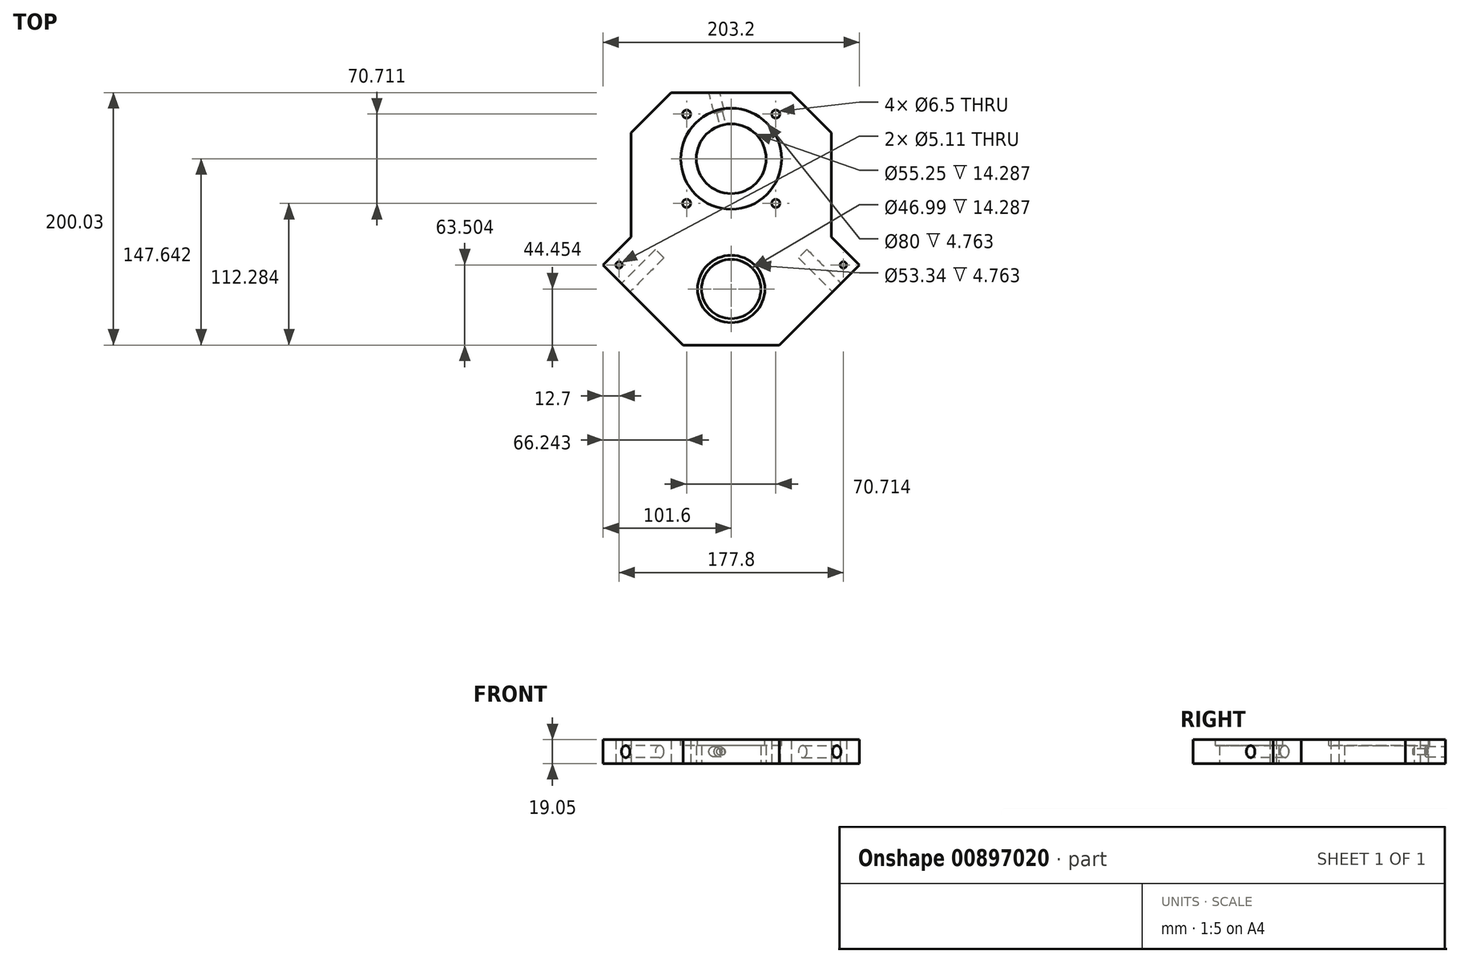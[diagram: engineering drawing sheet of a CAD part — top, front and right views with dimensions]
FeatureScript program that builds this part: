
annotation { "Feature Type Name" : "Feature", "Feature Type Description" : "" }
export const myFeature = defineFeature(function(context is Context, id is Id, definition is map)
    precondition{}
    {
        {
            var Q0;
            Q0=qCreatedBy(makeId("Top.planeOp"),FACE);
            var sketch = newSketch(context, id + "F0", { "sketchPlane" : qUnion([Q0])});
            skCircle(sketch, "E0", {"center": v(0, 19.05) * mm, "radius": 27.62 * mm});
            skPoint(sketch, "E0.centerSnap0", {"position": v(0, 71.44) * mm});
            skPoint(sketch, "E1", {"position": v(101.6, 0) * mm});
            skLineSegment(sketch, "E2", {"start": v(0, 71.44) * mm, "end": v(-47.63, 71.44) * mm});
            skLineSegment(sketch, "E3", {"start": v(-47.63, 71.44) * mm, "end": v(-79.38, 39.69) * mm});
            skPoint(sketch, "E4.orphan", {"position": v(-79.38, 71.44) * mm});
            skLineSegment(sketch, "E5", {"start": v(-79.38, 39.69) * mm, "end": v(-79.38, -42.86) * mm});
            skLineSegment(sketch, "E6", {"start": v(-101.6, -65.09) * mm, "end": v(-79.37, -42.86) * mm});
            skLineSegment(sketch, "E7", {"start": v(-101.6, -65.09) * mm, "end": v(-38.1, -128.59) * mm});
            skLineSegment(sketch, "E8", {"start": v(-38.1, -128.59) * mm, "end": v(0, -128.59) * mm});
            skLineSegment(sketch, "E9.MirrorCS", {"start": v(38.1, -128.59) * mm, "end": v(0, -128.59) * mm});
            skLineSegment(sketch, "E10.MirrorCS", {"start": v(101.6, -65.09) * mm, "end": v(38.1, -128.59) * mm});
            skLineSegment(sketch, "E11.MirrorCS", {"start": v(101.6, -65.09) * mm, "end": v(79.37, -42.86) * mm});
            skLineSegment(sketch, "E12.MirrorCS", {"start": v(79.38, 39.69) * mm, "end": v(79.38, -42.86) * mm});
            skLineSegment(sketch, "E13.MirrorCS", {"start": v(0, 71.44) * mm, "end": v(47.63, 71.44) * mm});
            skLineSegment(sketch, "E14.MirrorCS", {"start": v(47.63, 71.44) * mm, "end": v(79.38, 39.69) * mm});
            skCircle(sketch, "E15", {"center": v(-35.36, 54.4) * mm, "radius": 3.25 * mm});
            skCircle(sketch, "E16", {"center": v(-35.36, -16.3) * mm, "radius": 3.25 * mm});
            skCircle(sketch, "E17.MirrorC", {"center": v(35.36, 54.4) * mm, "radius": 3.25 * mm});
            skCircle(sketch, "E18.MirrorC", {"center": v(35.36, -16.3) * mm, "radius": 3.25 * mm});
            skCircle(sketch, "E19", {"center": v(0, -84.14) * mm, "radius": 23.5 * mm});
            skSolve(sketch);
        }
        {
            var Q0;
            Q0=makeQuery(id+"F0.imprint","IMPRINT",FACE,{"disambiguationData":[TD([[makeQuery(id+"F0.imprint","IMPRINT",EDGE,{"derivedFrom":sQuery(id+"F0.wireOp",EDGE,"E0")}),-1.0]])]});
            extrude(context, id + "F1", {"entities" : qUnion([Q0]), "depth" : 19.05 * mm, "offsetDistance" : 25.4 * mm});
        }
        {
            var Q0;
            Q0=makeQuery(id+"F1.opExtrude","CAP_FACE",FACE,{"disambiguationData":[OSD([sQuery(id+"F0.wireOp",EDGE,"E0"),sQuery(id+"F0.wireOp",EDGE,"E2"),sQuery(id+"F0.wireOp",EDGE,"E3"),sQuery(id+"F0.wireOp",EDGE,"E5"),sQuery(id+"F0.wireOp",EDGE,"E6"),sQuery(id+"F0.wireOp",EDGE,"E7"),sQuery(id+"F0.wireOp",EDGE,"E8"),sQuery(id+"F0.wireOp",EDGE,"E9.MirrorCS"),sQuery(id+"F0.wireOp",EDGE,"E10.MirrorCS"),sQuery(id+"F0.wireOp",EDGE,"E11.MirrorCS"),sQuery(id+"F0.wireOp",EDGE,"E12.MirrorCS"),sQuery(id+"F0.wireOp",EDGE,"E13.MirrorCS"),sQuery(id+"F0.wireOp",EDGE,"E14.MirrorCS"),sQuery(id+"F0.wireOp",EDGE,"Sg9kbkmI-cyti-gkXL-u0Fb-a4zstMvbkARu"),sQuery(id+"F0.wireOp",EDGE,"E15"),sQuery(id+"F0.wireOp",EDGE,"E16"),sQuery(id+"F0.wireOp",EDGE,"cdMgu5D0-0KZI-srT0-SeOJ-SRvMt6IrKFah"),sQuery(id+"F0.wireOp",EDGE,"E17.MirrorC"),sQuery(id+"F0.wireOp",EDGE,"d53a70e5-4a92-4dcf-ae8e-4d6e0ce8da4f1.MirrorC"),sQuery(id+"F0.wireOp",EDGE,"E18.MirrorC"),sQuery(id+"F0.wireOp",EDGE,"d53a70e5-4a92-4dcf-ae8e-4d6e0ce8da4f3.MirrorC"),sQuery(id+"F0.wireOp",EDGE,"E19")])],"isStart":false});
            var sketch = newSketch(context, id + "F2", { "sketchPlane" : qUnion([Q0])});
            skCircle(sketch, "E20", {"center": v(0, -84.14) * mm, "radius": 26.67 * mm});
            skCircle(sketch, "E21", {"center": v(0, 19.05) * mm, "radius": 40 * mm});
            skSolve(sketch);
        }
        {
            var Q0;
            Q0=makeQuery(id+"F2.imprint","IMPRINT",FACE,{"disambiguationData":[TD([[makeQuery(id+"F2.imprint","IMPRINT",EDGE,{"derivedFrom":sQuery(id+"F2.wireOp",EDGE,"E20")}),1.0]])]});
            var Q1;
            Q1=makeQuery(id+"F2.imprint","IMPRINT",FACE,{"disambiguationData":[TD([[makeQuery(id+"F2.imprint","IMPRINT",EDGE,{"derivedFrom":sQuery(id+"F2.wireOp",EDGE,"E21")}),1.0]])]});
            extrude(context, id + "F3", {"entities" : qUnion([Q0, Q1]), "operationType" : NewBodyOperationType.REMOVE, "oppositeDirection" : true, "depth" : 4.76 * mm, "offsetDistance" : 25.4 * mm});
        }
        {
            var Q0;
            Q0=makeQuery(id+"F1.opExtrude","SWEPT_FACE",FACE,{"disambiguationData":[OSD([sQuery(id+"F0.wireOp",EDGE,"E7")])]});
            var sketch = newSketch(context, id + "F4", { "sketchPlane" : qUnion([Q0])});
            skCircle(sketch, "E22", {"center": v(-0.42, 9.53) * mm, "radius": 4.76 * mm});
            skPoint(sketch, "E22.centerSnap0", {"position": v(-25.82, 9.53) * mm});
            skSolve(sketch);
        }
        {
            var Q0;
            Q0=makeQuery(id+"F4.imprint","IMPRINT",FACE,{"disambiguationData":[TD([[makeQuery(id+"F4.imprint","IMPRINT",EDGE,{"derivedFrom":sQuery(id+"F4.wireOp",EDGE,"E22")}),1.0]])]});
            extrude(context, id + "F5", {"entities" : qUnion([Q0]), "operationType" : NewBodyOperationType.REMOVE, "oppositeDirection" : true, "depth" : 38.1 * mm, "offsetDistance" : 25.4 * mm});
        }
        {
            var Q0;
            Q0=makeQuery(id+"F1.opExtrude","SWEPT_FACE",FACE,{"disambiguationData":[OSD([sQuery(id+"F0.wireOp",EDGE,"E10.MirrorCS")])]});
            var sketch = newSketch(context, id + "F6", { "sketchPlane" : qUnion([Q0])});
            skCircle(sketch, "E23", {"center": v(0.42, 9.53) * mm, "radius": 4.76 * mm});
            skPoint(sketch, "E23.centerSnap0", {"position": v(25.82, 9.53) * mm});
            skSolve(sketch);
        }
        {
            var Q0;
            Q0=makeQuery(id+"F6.imprint","IMPRINT",FACE,{"disambiguationData":[TD([[makeQuery(id+"F6.imprint","IMPRINT",EDGE,{"derivedFrom":sQuery(id+"F6.wireOp",EDGE,"E23")}),1.0]])]});
            extrude(context, id + "F7", {"entities" : qUnion([Q0]), "operationType" : NewBodyOperationType.REMOVE, "oppositeDirection" : true, "depth" : 38.1 * mm, "offsetDistance" : 25.4 * mm});
        }
        {
            var Q0;
            Q0=makeQuery(id+"F1.opExtrude","SWEPT_FACE",FACE,{"disambiguationData":[OSD([sQuery(id+"F0.wireOp",EDGE,"E2"),sQuery(id+"F0.wireOp",EDGE,"E13.MirrorCS")])]});
            var sketch = newSketch(context, id + "F8", { "sketchPlane" : qUnion([Q0])});
            skCircle(sketch, "E24", {"center": v(13.34, 9.53) * mm, "radius": 2.38 * mm});
            skPoint(sketch, "E24.centerSnap0", {"position": v(47.63, 9.53) * mm});
            skLineSegment(sketch, "E25", {"start": v(13.34, 9.53) * mm, "end": v(13.34, 0) * mm});
            skSolve(sketch);
        }
        {
            var Q0;
            Q0=makeQuery(id+"F1.opExtrude","CAP_FACE",FACE,{"disambiguationData":[OSD([sQuery(id+"F0.wireOp",EDGE,"E0"),sQuery(id+"F0.wireOp",EDGE,"E2"),sQuery(id+"F0.wireOp",EDGE,"E3"),sQuery(id+"F0.wireOp",EDGE,"E5"),sQuery(id+"F0.wireOp",EDGE,"E6"),sQuery(id+"F0.wireOp",EDGE,"E7"),sQuery(id+"F0.wireOp",EDGE,"E8"),sQuery(id+"F0.wireOp",EDGE,"E9.MirrorCS"),sQuery(id+"F0.wireOp",EDGE,"E10.MirrorCS"),sQuery(id+"F0.wireOp",EDGE,"E11.MirrorCS"),sQuery(id+"F0.wireOp",EDGE,"E12.MirrorCS"),sQuery(id+"F0.wireOp",EDGE,"E13.MirrorCS"),sQuery(id+"F0.wireOp",EDGE,"E14.MirrorCS"),sQuery(id+"F0.wireOp",EDGE,"Sg9kbkmI-cyti-gkXL-u0Fb-a4zstMvbkARu"),sQuery(id+"F0.wireOp",EDGE,"E15"),sQuery(id+"F0.wireOp",EDGE,"E16"),sQuery(id+"F0.wireOp",EDGE,"cdMgu5D0-0KZI-srT0-SeOJ-SRvMt6IrKFah"),sQuery(id+"F0.wireOp",EDGE,"E17.MirrorC"),sQuery(id+"F0.wireOp",EDGE,"d53a70e5-4a92-4dcf-ae8e-4d6e0ce8da4f1.MirrorC"),sQuery(id+"F0.wireOp",EDGE,"E18.MirrorC"),sQuery(id+"F0.wireOp",EDGE,"d53a70e5-4a92-4dcf-ae8e-4d6e0ce8da4f3.MirrorC"),sQuery(id+"F0.wireOp",EDGE,"E19"),sQuery(id+"F0.wireOp",EDGE,"SRUyxVlJ-cAlB-7OkV-Ly4u-9J5VbLR8ibiF")])],"isStart":false});
            var sketch = newSketch(context, id + "F9", { "sketchPlane" : qUnion([Q0])});
            skLineSegment(sketch, "E26", {"start": v(0, 19.05) * mm, "end": v(-13.34, 71.44) * mm});
            skSolve(sketch);
        }
        {
            var Q0;
            Q0=sQuery(id+"F8.wireOp",VERTEX,"E25.start");
            var Q1;
            Q1=sQuery(id+"F8.wireOp",VERTEX,"E25.end");
            var Q2;
            Q2=sQuery(id+"F9.wireOp",VERTEX,"E26.start");
            cPlane(context, id + "F10", {"entities" : qUnion([Q0, Q1, Q2]), "cplaneType" : CPlaneType.THREE_POINT, "offset" : 25.4 * mm, "width" : 152.4 * mm, "height" : 152.4 * mm});
        }
        {
            var Q0;
            Q0=qCreatedBy(id+"F10.planeOp",FACE);
            var sketch = newSketch(context, id + "F11", { "sketchPlane" : qUnion([Q0])});
            skLineSegment(sketch, "E27", {"start": v(109.63, 9.53) * mm, "end": v(109.63, 11.9) * mm});
            skLineSegment(sketch, "E28", {"start": v(109.63, 9.53) * mm, "end": v(43.12, 9.53) * mm});
            skLineSegment(sketch, "E29", {"start": v(43.12, 9.53) * mm, "end": v(43.12, 11.9) * mm});
            skLineSegment(sketch, "E30", {"start": v(43.12, 11.9) * mm, "end": v(109.63, 11.9) * mm});
            skSolve(sketch);
        }
        {
            var Q0;
            Q0 = qSketchRegion(id + "F11", true);
            var Q1;
            Q1=sQuery(id+"F11.wireOp",EDGE,"E28");
            revolve(context, id + "F12", {"operationType" : NewBodyOperationType.REMOVE, "surfaceOperationType" : NewSurfaceOperationType.NEW, "entities" : qUnion([Q0]), "axis" : qUnion([Q1]), "revolveType" : RevolveType.FULL, "oppositeDirection" : true});
        }
        {
            var Q0;
            Q0=qCreatedBy(id+"F10.planeOp",FACE);
            var sketch = newSketch(context, id + "F13", { "sketchPlane" : qUnion([Q0])});
            skLineSegment(sketch, "E31", {"start": v(72.52, 13.74) * mm, "end": v(72.52, 9.53) * mm});
            skLineSegment(sketch, "E32", {"start": v(72.52, 13.74) * mm, "end": v(56.77, 13.74) * mm});
            skLineSegment(sketch, "E33", {"start": v(56.77, 13.74) * mm, "end": v(56.77, 9.53) * mm});
            skLineSegment(sketch, "E34", {"start": v(56.77, 9.53) * mm, "end": v(72.52, 9.53) * mm});
            skLineSegment(sketch, "E35", {"start": v(72.52, 13.74) * mm, "end": v(103.66, 13.74) * mm});
            skLineSegment(sketch, "E36", {"start": v(103.66, 13.74) * mm, "end": v(103.66, 9.53) * mm});
            skLineSegment(sketch, "E37", {"start": v(103.66, 9.53) * mm, "end": v(72.52, 9.53) * mm});
            skSolve(sketch);
        }
        {
            var Q0;
            Q0 = qSketchRegion(id + "F13", true);
            var Q1;
            Q1=sQuery(id+"F13.wireOp",EDGE,"E34");
            revolve(context, id + "F14", {"operationType" : NewBodyOperationType.REMOVE, "surfaceOperationType" : NewSurfaceOperationType.NEW, "entities" : qUnion([Q0]), "axis" : qUnion([Q1]), "revolveType" : RevolveType.FULL, "oppositeDirection" : true});
        }
        {
            var Q0;
            Q0=makeQuery(id+"F1.opExtrude","CAP_FACE",FACE,{"disambiguationData":[OSD([sQuery(id+"F0.wireOp",EDGE,"E0"),sQuery(id+"F0.wireOp",EDGE,"E2"),sQuery(id+"F0.wireOp",EDGE,"E3"),sQuery(id+"F0.wireOp",EDGE,"E5"),sQuery(id+"F0.wireOp",EDGE,"E6"),sQuery(id+"F0.wireOp",EDGE,"E7"),sQuery(id+"F0.wireOp",EDGE,"E8"),sQuery(id+"F0.wireOp",EDGE,"E9.MirrorCS"),sQuery(id+"F0.wireOp",EDGE,"E10.MirrorCS"),sQuery(id+"F0.wireOp",EDGE,"E11.MirrorCS"),sQuery(id+"F0.wireOp",EDGE,"E12.MirrorCS"),sQuery(id+"F0.wireOp",EDGE,"E13.MirrorCS"),sQuery(id+"F0.wireOp",EDGE,"E14.MirrorCS"),sQuery(id+"F0.wireOp",EDGE,"E15"),sQuery(id+"F0.wireOp",EDGE,"E16"),sQuery(id+"F0.wireOp",EDGE,"E17.MirrorC"),sQuery(id+"F0.wireOp",EDGE,"E18.MirrorC"),sQuery(id+"F0.wireOp",EDGE,"E19")])],"isStart":true});
            var sketch = newSketch(context, id + "F15", { "sketchPlane" : qUnion([Q0])});
            skPoint(sketch, "E38", {"position": v(-88.9, 65.09) * mm});
            skPoint(sketch, "E39.MirrorP", {"position": v(88.9, 65.09) * mm});
            skSolve(sketch);
        }
        {
            var Q0;
            Q0=sQuery(id+"F15.wireOp",VERTEX,"E38");
            var Q1;
            Q1=sQuery(id+"F15.wireOp",VERTEX,"E39.MirrorP");
            var Q2;
            Q2=makeQuery(id+"F1.opExtrude","SWEPT_BODY",BODY,{"disambiguationData":[OSD([sQuery(id+"F0.wireOp",EDGE,"E0"),sQuery(id+"F0.wireOp",EDGE,"E2"),sQuery(id+"F0.wireOp",EDGE,"E3"),sQuery(id+"F0.wireOp",EDGE,"E5"),sQuery(id+"F0.wireOp",EDGE,"E6"),sQuery(id+"F0.wireOp",EDGE,"E7"),sQuery(id+"F0.wireOp",EDGE,"E8"),sQuery(id+"F0.wireOp",EDGE,"E9.MirrorCS"),sQuery(id+"F0.wireOp",EDGE,"E10.MirrorCS"),sQuery(id+"F0.wireOp",EDGE,"E11.MirrorCS"),sQuery(id+"F0.wireOp",EDGE,"E12.MirrorCS"),sQuery(id+"F0.wireOp",EDGE,"E13.MirrorCS"),sQuery(id+"F0.wireOp",EDGE,"E14.MirrorCS"),sQuery(id+"F0.wireOp",EDGE,"E15"),sQuery(id+"F0.wireOp",EDGE,"E16"),sQuery(id+"F0.wireOp",EDGE,"E17.MirrorC"),sQuery(id+"F0.wireOp",EDGE,"E18.MirrorC"),sQuery(id+"F0.wireOp",EDGE,"E19")])]});
            hole(context, id + "F16", {"style" : HoleStyle.SIMPLE, "endStyle" : HoleEndStyle.THROUGH, "standardTappedOrClearance" : lookupTablePath({ "standard" : "ANSI", "engagement" : "75%", "pitch" : "20 tpi", "size" : "1/4", "type" : "Tapped" }), "standardBlindInLast" : lookupTablePath({ "fit" : "Free", "standard" : "ANSI", "engagement" : "75%", "pitch" : "20 tpi", "size" : "1/4", "type" : "Clearance & tapped" }), "holeDiameter" : 5.1 * mm, "majorDiameter" : 6.35 * mm, "showTappedDepth" : true, "isTappedThrough" : true, "tappedDepth" : 19.05 * mm, "tapClearance" : 2, "startFromSketch" : true, "locations" : qUnion([Q0, Q1]), "scope" : qUnion([Q2])});
        }
    });
